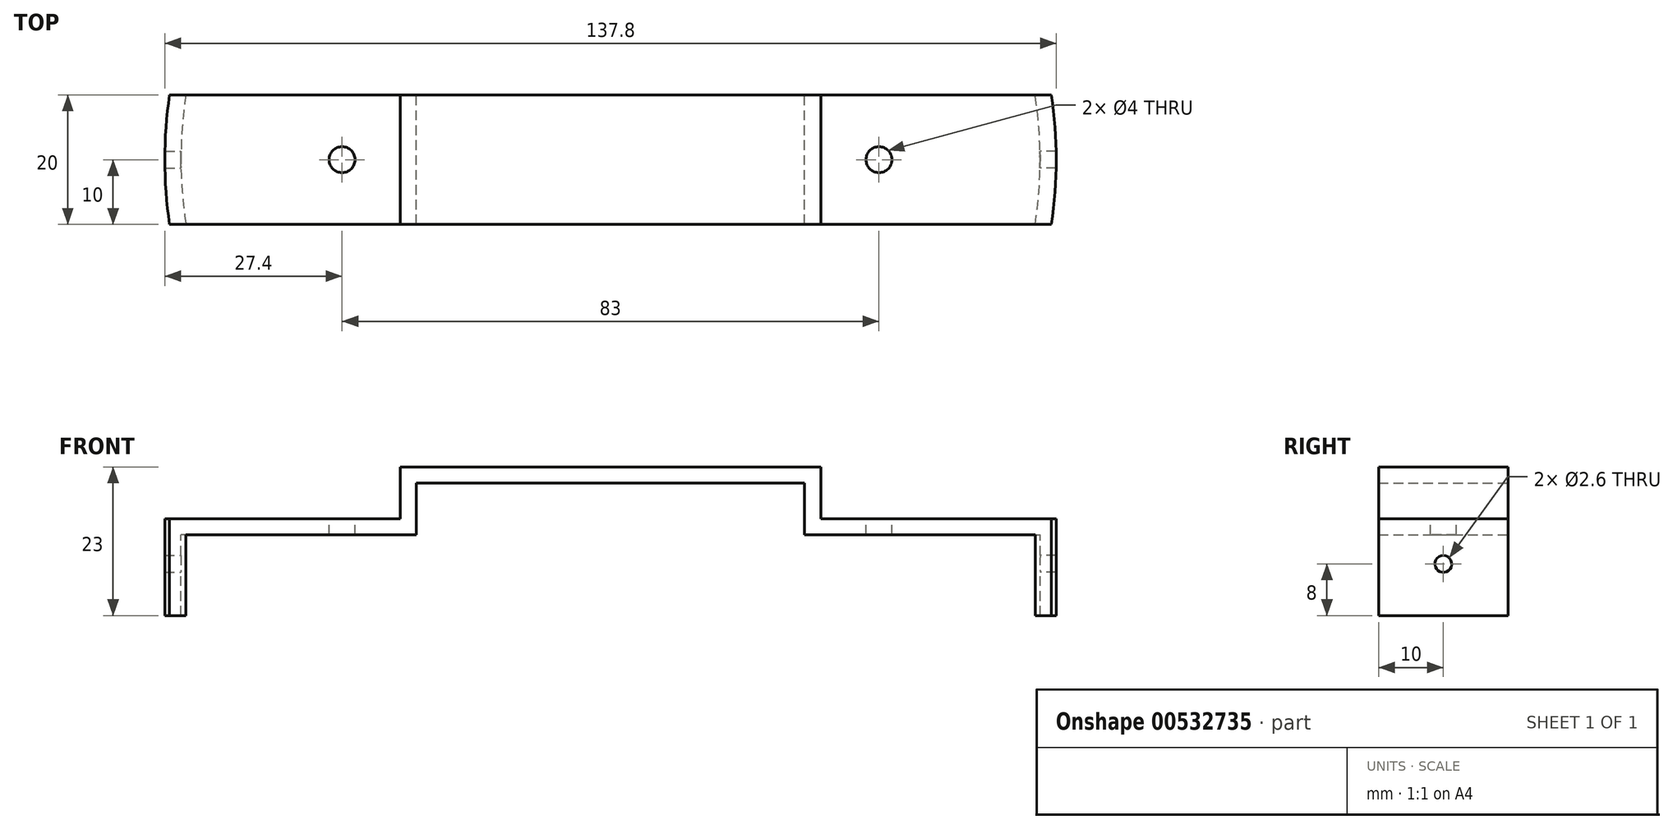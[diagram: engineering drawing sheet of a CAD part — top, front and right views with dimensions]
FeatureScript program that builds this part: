
annotation { "Feature Type Name" : "Feature", "Feature Type Description" : "" }
export const myFeature = defineFeature(function(context is Context, id is Id, definition is map)
    precondition{}
    {
        {
            var Q0;
            Q0=qCreatedBy(makeId("Front.planeOp"),FACE);
            var sketch = newSketch(context, id + "F0", { "sketchPlane" : qUnion([Q0])});
            skLineSegment(sketch, "E0", {"start": v(0, 0) * mm, "end": v(32.5, 0) * mm});
            skLineSegment(sketch, "E1", {"start": v(32.5, 0) * mm, "end": v(32.5, -8) * mm});
            skLineSegment(sketch, "E2", {"start": v(32.5, -8) * mm, "end": v(68.9, -8) * mm});
            skLineSegment(sketch, "E3", {"start": v(68.9, -8) * mm, "end": v(68.9, -23) * mm});
            skLineSegment(sketch, "E4.0", {"start": v(66.4, -10.5) * mm, "end": v(66.4, -23) * mm});
            skLineSegment(sketch, "E4.1", {"start": v(30, -10.5) * mm, "end": v(66.4, -10.5) * mm});
            skLineSegment(sketch, "E4.2", {"start": v(30, -2.5) * mm, "end": v(30, -10.5) * mm});
            skLineSegment(sketch, "E4.3", {"start": v(0, -2.5) * mm, "end": v(30, -2.5) * mm});
            skLineSegment(sketch, "E5", {"start": v(0, 0) * mm, "end": v(0, -2.5) * mm});
            skLineSegment(sketch, "E6", {"start": v(66.4, -23) * mm, "end": v(68.9, -23) * mm});
            skSolve(sketch);
        }
        {
            var Q0;
            Q0 = qSketchRegion(id + "F0", true);
            extrude(context, id + "F1", {"entities" : qUnion([Q0]), "endBound" : BoundingType.SYMMETRIC, "depth" : 20 * mm, "offsetDistance" : 25 * mm});
        }
        {
            var Q0;
            Q0=qCreatedBy(makeId("Top.planeOp"),FACE);
            var sketch = newSketch(context, id + "F2", { "sketchPlane" : qUnion([Q0])});
            skCircle(sketch, "E7", {"center": v(41.5, 0) * mm, "radius": 2 * mm});
            skLineSegment(sketch, "E8", {"start": v(0, 0) * mm, "end": v(41.5, 0) * mm, "construction": true});
            skSolve(sketch);
        }
        {
            var Q0;
            Q0 = qSketchRegion(id + "F2", true);
            extrude(context, id + "F3", {"entities" : qUnion([Q0]), "operationType" : NewBodyOperationType.REMOVE, "endBound" : BoundingType.THROUGH_ALL, "oppositeDirection" : true, "depth" : 25 * mm, "offsetDistance" : 25 * mm});
        }
        {
            var Q0;
            Q0=makeQuery(id+"F1.opExtrude","SWEPT_FACE",FACE,{"disambiguationData":[OSD([sQuery(id+"F0.wireOp",EDGE,"E2")])]});
            var sketch = newSketch(context, id + "F4", { "sketchPlane" : qUnion([Q0])});
            skLineSegment(sketch, "E9.0", {"start": v(32.5, 10) * mm, "end": v(68.9, 10) * mm});
            skLineSegment(sketch, "E9.1", {"start": v(32.5, -10) * mm, "end": v(68.9, -10) * mm});
            skArc(sketch, "E10", {"start": v(68.17, -10) * mm, "mid": v(68.9, 0) * mm, "end": v(68.17, 10) * mm});
            skArc(sketch, "E11", {"start": v(65.64, -10) * mm, "mid": v(66.4, 0) * mm, "end": v(65.64, 10) * mm});
            skLineSegment(sketch, "E12", {"start": v(68.9, 10) * mm, "end": v(70.9, 10) * mm});
            skLineSegment(sketch, "E13", {"start": v(70.9, 10) * mm, "end": v(70.9, -10) * mm});
            skLineSegment(sketch, "E14", {"start": v(70.9, -10) * mm, "end": v(68.9, -10) * mm});
            skSolve(sketch);
        }
        {
            var Q0;
            {var subQ1=sQuery(id+"F4.wireOp",EDGE,"E12");Q0=makeQuery(id+"F4.imprint","IMPRINT",FACE,{"disambiguationData":[TD([[makeQuery(id+"F4.imprint","IMPRINT",EDGE,{"derivedFrom":subQ1}),-1.0]])]});}
            var Q1;
            {var subQ0=sQuery(id+"F4.wireOp",EDGE,"E9.1");var subQ3=sQuery(id+"F4.wireOp",EDGE,"E10");var subQ4=makeQuery(id+"F4.imprint","INTERSECT",VERTEX,{"derivedFrom":[subQ0,subQ3]});Q1=makeQuery(id+"F4.imprint","IMPRINT",FACE,{"disambiguationData":[TD([[makeQuery(id+"F4.imprint","IMPRINT",EDGE,{"disambiguationData":[TD([[subQ4,-1.0]])],"derivedFrom":subQ3}),-1.0]])]});}
            var Q2;
            {var subQ0=sQuery(id+"F4.wireOp",EDGE,"E9.0");var subQ3=sQuery(id+"F4.wireOp",EDGE,"E10");var subQ4=makeQuery(id+"F4.imprint","INTERSECT",VERTEX,{"derivedFrom":[subQ0,subQ3]});Q2=makeQuery(id+"F4.imprint","IMPRINT",FACE,{"disambiguationData":[TD([[makeQuery(id+"F4.imprint","IMPRINT",EDGE,{"disambiguationData":[TD([[subQ4,1.0]])],"derivedFrom":subQ3}),-1.0]])]});}
            extrude(context, id + "F5", {"entities" : qUnion([Q0, Q1, Q2]), "operationType" : NewBodyOperationType.REMOVE, "endBound" : BoundingType.THROUGH_ALL, "oppositeDirection" : true, "depth" : 25 * mm, "offsetDistance" : 25 * mm});
        }
        {
            var Q0;
            {var subQ6=sQuery(id+"F4.wireOp",EDGE,"E11");Q0=makeQuery(id+"F4.imprint","IMPRINT",FACE,{"disambiguationData":[TD([[makeQuery(id+"F4.imprint","IMPRINT",EDGE,{"derivedFrom":subQ6}),-1.0]])]});}
            var Q1;
            Q1=makeQuery(id+"F1.opExtrude","SWEPT_FACE",FACE,{"disambiguationData":[OSD([sQuery(id+"F0.wireOp",EDGE,"E6")])]});
            extrude(context, id + "F6", {"entities" : qUnion([Q0]), "operationType" : NewBodyOperationType.ADD, "endBound" : BoundingType.UP_TO_SURFACE, "oppositeDirection" : true, "depth" : 25 * mm, "endBoundEntityFace" : qUnion([Q1]), "offsetDistance" : 25 * mm});
        }
        {
            var Q0;
            Q0=qCreatedBy(makeId("Right.planeOp"),FACE);
            var sketch = newSketch(context, id + "F7", { "sketchPlane" : qUnion([Q0])});
            skLineSegment(sketch, "E15.0", {"start": v(-10, -8) * mm, "end": v(10, -8) * mm, "construction": true});
            skLineSegment(sketch, "E16", {"start": v(0, -8) * mm, "end": v(0, -15) * mm, "construction": true});
            skCircle(sketch, "E17", {"center": v(0, -15) * mm, "radius": 1.3 * mm});
            skSolve(sketch);
        }
        {
            var Q0;
            Q0 = qSketchRegion(id + "F7", true);
            extrude(context, id + "F8", {"entities" : qUnion([Q0]), "operationType" : NewBodyOperationType.REMOVE, "endBound" : BoundingType.THROUGH_ALL, "depth" : 25 * mm, "offsetDistance" : 25 * mm});
        }
        {
            var Q0;
            Q0=makeQuery(id+"F1.opExtrude","SWEPT_BODY",BODY,{"disambiguationData":[OSD([sQuery(id+"F0.wireOp",EDGE,"E0"),sQuery(id+"F0.wireOp",EDGE,"E1"),sQuery(id+"F0.wireOp",EDGE,"E2"),sQuery(id+"F0.wireOp",EDGE,"E3"),sQuery(id+"F0.wireOp",EDGE,"E4.0"),sQuery(id+"F0.wireOp",EDGE,"E4.1"),sQuery(id+"F0.wireOp",EDGE,"E4.2"),sQuery(id+"F0.wireOp",EDGE,"E4.3"),sQuery(id+"F0.wireOp",EDGE,"E5"),sQuery(id+"F0.wireOp",EDGE,"E6")])]});
            var Q1;
            Q1=qCreatedBy(makeId("Right.planeOp"),FACE);
            mirror(context, id + "F9", {"operationType" : NewBodyOperationType.ADD, "entities" : qUnion([Q0]), "mirrorPlane" : qUnion([Q1])});
        }
    });
